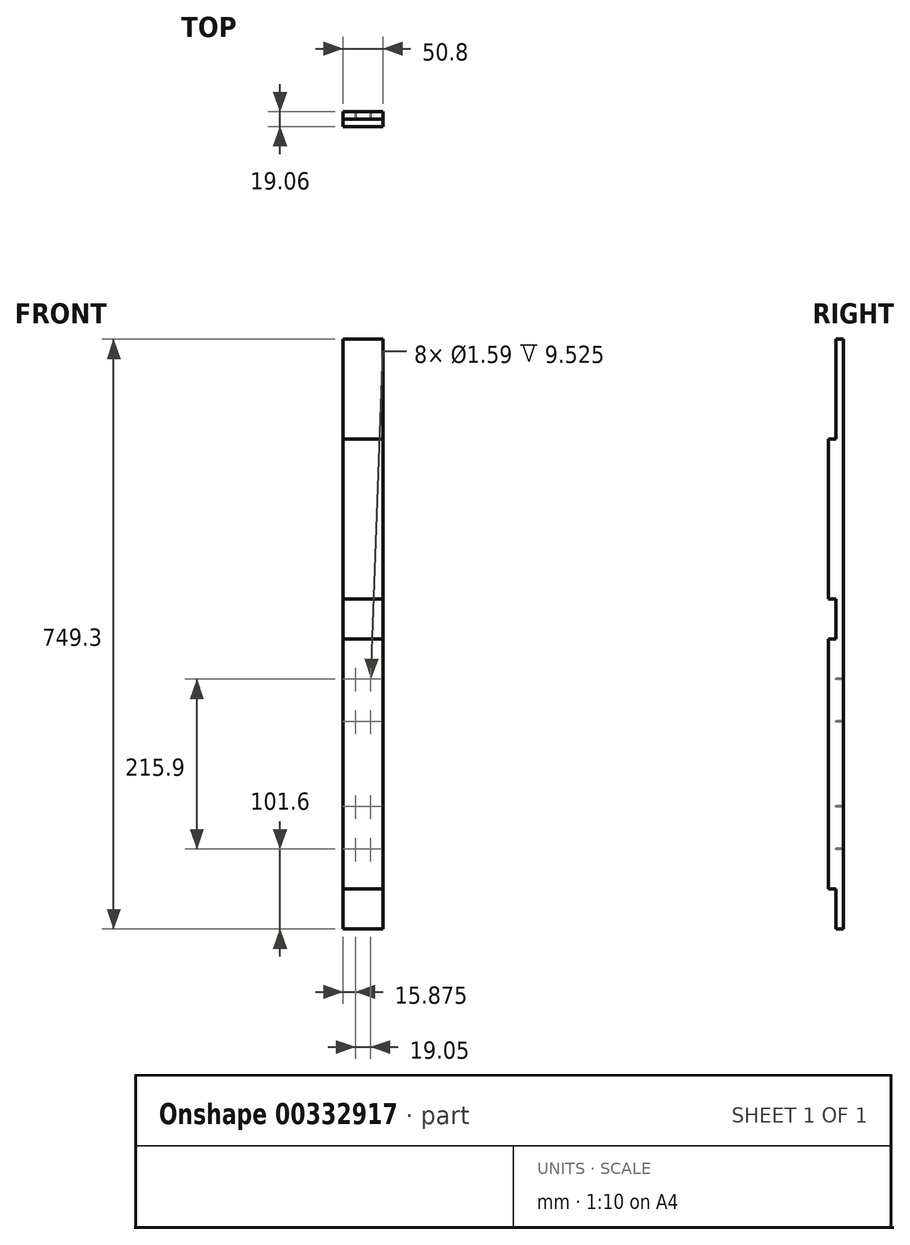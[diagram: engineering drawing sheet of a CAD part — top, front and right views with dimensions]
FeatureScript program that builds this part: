
annotation { "Feature Type Name" : "Feature", "Feature Type Description" : "" }
export const myFeature = defineFeature(function(context is Context, id is Id, definition is map)
    precondition{}
    {
        {
            var Q0;
            Q0=qCreatedBy(makeId("Top.planeOp"),FACE);
            var sketch = newSketch(context, id + "F0", { "sketchPlane" : qUnion([Q0])});
            skLineSegment(sketch, "E0.bottom", {"start": v(25.4, 9.53) * mm, "end": v(-25.4, 9.53) * mm});
            skLineSegment(sketch, "E0.top", {"start": v(25.4, -9.53) * mm, "end": v(-25.4, -9.53) * mm});
            skLineSegment(sketch, "E0.left", {"start": v(25.4, 9.53) * mm, "end": v(25.4, -9.52) * mm});
            skLineSegment(sketch, "E0.right", {"start": v(-25.4, 9.53) * mm, "end": v(-25.4, -9.53) * mm});
            skPoint(sketch, "E0.middle", {"position": v(0, 0) * mm});
            skSolve(sketch);
        }
        {
            var Q0;
            Q0=makeQuery(id+"F0.imprint","IMPRINT",FACE,{"disambiguationData":[TD([[makeQuery(id+"F0.imprint","IMPRINT",EDGE,{"derivedFrom":sQuery(id+"F0.wireOp",EDGE,"E0.bottom")}),1.0]])]});
            extrude(context, id + "F1", {"entities" : qUnion([Q0]), "depth" : 749.3 * mm});
        }
        {
            var Q0;
            Q0=qCreatedBy(makeId("Front.planeOp"),FACE);
            var sketch = newSketch(context, id + "F2", { "sketchPlane" : qUnion([Q0])});
            skLineSegment(sketch, "E1.bottom", {"start": v(-38.77, 0) * mm, "end": v(83.66, 0) * mm});
            skLineSegment(sketch, "E1.top", {"start": v(-38.77, 50.8) * mm, "end": v(83.66, 50.8) * mm});
            skLineSegment(sketch, "E1.left", {"start": v(-38.77, 0) * mm, "end": v(-38.77, 50.8) * mm});
            skLineSegment(sketch, "E1.right", {"start": v(83.66, 0) * mm, "end": v(83.66, 50.8) * mm});
            skLineSegment(sketch, "E2.bottom", {"start": v(-44.21, 368.3) * mm, "end": v(49.65, 368.3) * mm});
            skLineSegment(sketch, "E2.top", {"start": v(-44.21, 419.1) * mm, "end": v(49.65, 419.1) * mm});
            skLineSegment(sketch, "E2.left", {"start": v(-44.21, 368.3) * mm, "end": v(-44.21, 419.1) * mm});
            skLineSegment(sketch, "E2.right", {"start": v(49.65, 368.3) * mm, "end": v(49.65, 419.1) * mm});
            skLineSegment(sketch, "E3.bottom", {"start": v(-210.36, 622.3) * mm, "end": v(132.8, 622.3) * mm});
            skLineSegment(sketch, "E3.top", {"start": v(-210.36, 749.3) * mm, "end": v(132.8, 749.3) * mm});
            skLineSegment(sketch, "E3.left", {"start": v(-210.36, 622.3) * mm, "end": v(-210.36, 749.3) * mm});
            skLineSegment(sketch, "E3.right", {"start": v(132.8, 622.3) * mm, "end": v(132.8, 749.3) * mm});
            skSolve(sketch);
        }
        {
            var Q0;
            Q0=qSketchRegion(id+"F2",true);
            extrude(context, id + "F3", {"entities" : qUnion([Q0]), "operationType" : NewBodyOperationType.REMOVE, "depth" : 25.4 * mm});
        }
        {
            var Q0;
            Q0=qCreatedBy(makeId("Front.planeOp"),FACE);
            var sketch = newSketch(context, id + "F4", { "sketchPlane" : qUnion([Q0])});
            skCircle(sketch, "E4", {"center": v(9.52, 101.6) * mm, "radius": 0.8 * mm});
            skCircle(sketch, "E5", {"center": v(9.52, 155.58) * mm, "radius": 0.8 * mm});
            skCircle(sketch, "E6", {"center": v(9.52, 263.53) * mm, "radius": 0.8 * mm});
            skCircle(sketch, "E7", {"center": v(9.52, 317.5) * mm, "radius": 0.8 * mm});
            skLineSegment(sketch, "E8", {"start": v(0, 0) * mm, "end": v(0, 1192.46) * mm, "construction": true});
            skLineSegment(sketch, "E9.bottom", {"start": v(9.52, 101.6) * mm, "end": v(-9.52, 101.6) * mm, "construction": true});
            skLineSegment(sketch, "E9.top", {"start": v(9.52, 317.5) * mm, "end": v(-9.53, 317.5) * mm, "construction": true});
            skLineSegment(sketch, "E9.left", {"start": v(9.53, 101.6) * mm, "end": v(9.52, 317.5) * mm, "construction": true});
            skLineSegment(sketch, "E9.right", {"start": v(-9.52, 101.6) * mm, "end": v(-9.53, 317.5) * mm, "construction": true});
            skCircle(sketch, "E10", {"center": v(-9.53, 263.53) * mm, "radius": 0.8 * mm});
            skCircle(sketch, "E11", {"center": v(-9.53, 317.5) * mm, "radius": 0.8 * mm});
            skCircle(sketch, "E12", {"center": v(-9.52, 101.6) * mm, "radius": 0.8 * mm});
            skCircle(sketch, "E13", {"center": v(-9.52, 155.58) * mm, "radius": 0.8 * mm});
            skSolve(sketch);
        }
        {
            var Q0;
            Q0=qSketchRegion(id+"F4",true);
            extrude(context, id + "F5", {"entities" : qUnion([Q0]), "operationType" : NewBodyOperationType.REMOVE, "oppositeDirection" : true, "depth" : 25.4 * mm});
        }
    });
